FCSTD DOCUMENT  (FreeCAD 0.21R33771 (Git))
Label: drift2
License: All rights reserved
LicenseURL: https://en.wikipedia.org/wiki/All_rights_reserved
objects: Sketcher::SketchObject×5, Part::Loft×1
note: 6 computed .brp shape members not serialized (recipe doc carries the construction recipe); baked Part::Feature solids carry a one-line shape summary decoded from their .brp

FEATURE [Sketcher::SketchObject] Sketch  label="Sketch_s20_50x50"
  FullyConstrained = true
  sketch-geometry (5):
    g0: LineSegment StartX=-25 StartY=25 StartZ=0 EndX=-25 EndY=-25 EndZ=0
    g1: LineSegment StartX=-25 StartY=-25 StartZ=0 EndX=25 EndY=-25 EndZ=0
    g2: LineSegment StartX=25 StartY=-25 StartZ=0 EndX=25 EndY=25 EndZ=0
    g3: LineSegment StartX=25 StartY=25 StartZ=0 EndX=-25 EndY=25 EndZ=0
    g4: GeomPoint X=1e-16 Y=0 Z=0
  constraints (12):
    c: Coincident(g0,g1)
    c: Coincident(g1,g2)
    c: Coincident(g2,g3)
    c: Coincident(g3,g0)
    c: Horizontal(g1)
    c: Horizontal(g3)
    c: Vertical(g0)
    c: Vertical(g2)
    c: Symmetric(g1,g0,g4)
    c: Coincident(g4,g-1)
    c: Distance(g2) = 50
    c: Distance(g3) = 50
FEATURE [Sketcher::SketchObject] Sketch001  label="Sketch_s25_40x40"
  FullyConstrained = true
  Placement = pos=(0,0,5000) rot=(0,0,1;0rad)
  sketch-geometry (5):
    g0: LineSegment StartX=-20 StartY=20 StartZ=0 EndX=-20 EndY=-20 EndZ=0
    g1: LineSegment StartX=-20 StartY=-20 StartZ=0 EndX=20 EndY=-20 EndZ=0
    g2: LineSegment StartX=20 StartY=-20 StartZ=0 EndX=20 EndY=20 EndZ=0
    g3: LineSegment StartX=20 StartY=20 StartZ=0 EndX=-20 EndY=20 EndZ=0
    g4: GeomPoint X=1e-16 Y=1e-16 Z=0
  constraints (12):
    c: Coincident(g0,g1)
    c: Coincident(g1,g2)
    c: Coincident(g2,g3)
    c: Coincident(g3,g0)
    c: Horizontal(g1)
    c: Horizontal(g3)
    c: Vertical(g0)
    c: Vertical(g2)
    c: Symmetric(g1,g0,g4)
    c: Coincident(g4,g-1)
    c: Distance(g2) = 40
    c: Distance(g3) = 40
FEATURE [Sketcher::SketchObject] Sketch002  label="Sketch_s30_40x40"
  FullyConstrained = true
  Placement = pos=(0,0,10000) rot=(0,0,1;0rad)
  sketch-geometry (5):
    g0: LineSegment StartX=-20 StartY=20 StartZ=0 EndX=-20 EndY=-20 EndZ=0
    g1: LineSegment StartX=-20 StartY=-20 StartZ=0 EndX=20 EndY=-20 EndZ=0
    g2: LineSegment StartX=20 StartY=-20 StartZ=0 EndX=20 EndY=20 EndZ=0
    g3: LineSegment StartX=20 StartY=20 StartZ=0 EndX=-20 EndY=20 EndZ=0
    g4: GeomPoint X=-1e-16 Y=0 Z=0
  constraints (12):
    c: Coincident(g0,g1)
    c: Coincident(g1,g2)
    c: Coincident(g2,g3)
    c: Coincident(g3,g0)
    c: Horizontal(g1)
    c: Horizontal(g3)
    c: Vertical(g0)
    c: Vertical(g2)
    c: Symmetric(g1,g0,g4)
    c: Coincident(g4,g-1)
    c: Distance(g2) = 40
    c: Distance(g3) = 40
FEATURE [Sketcher::SketchObject] Sketch003  label="Sketch_s35_20x20"
  FullyConstrained = true
  Placement = pos=(0,0,15000) rot=(0,0,1;0rad)
  sketch-geometry (5):
    g0: LineSegment StartX=-10 StartY=10 StartZ=0 EndX=-10 EndY=-10 EndZ=0
    g1: LineSegment StartX=-10 StartY=-10 StartZ=0 EndX=10 EndY=-10 EndZ=0
    g2: LineSegment StartX=10 StartY=-10 StartZ=0 EndX=10 EndY=10 EndZ=0
    g3: LineSegment StartX=10 StartY=10 StartZ=0 EndX=-10 EndY=10 EndZ=0
    g4: GeomPoint X=0 Y=0 Z=0
  constraints (12):
    c: Coincident(g0,g1)
    c: Coincident(g1,g2)
    c: Coincident(g2,g3)
    c: Coincident(g3,g0)
    c: Horizontal(g1)
    c: Horizontal(g3)
    c: Vertical(g0)
    c: Vertical(g2)
    c: Symmetric(g1,g0,g4)
    c: Coincident(g4,g-1)
    c: Distance(g2) = 20
    c: Distance(g3) = 20
FEATURE [Sketcher::SketchObject] Sketch004  label="Sketch_s50_20x20"
  FullyConstrained = true
  Placement = pos=(0,0,30000) rot=(0,0,1;0rad)
  sketch-geometry (5):
    g0: LineSegment StartX=-10 StartY=10 StartZ=0 EndX=-10 EndY=-10 EndZ=0
    g1: LineSegment StartX=-10 StartY=-10 StartZ=0 EndX=10 EndY=-10 EndZ=0
    g2: LineSegment StartX=10 StartY=-10 StartZ=0 EndX=10 EndY=10 EndZ=0
    g3: LineSegment StartX=10 StartY=10 StartZ=0 EndX=-10 EndY=10 EndZ=0
    g4: GeomPoint X=0 Y=0 Z=0
  constraints (12):
    c: Coincident(g0,g1)
    c: Coincident(g1,g2)
    c: Coincident(g2,g3)
    c: Coincident(g3,g0)
    c: Horizontal(g1)
    c: Horizontal(g3)
    c: Vertical(g0)
    c: Vertical(g2)
    c: Symmetric(g1,g0,g4)
    c: Coincident(g4,g-1)
    c: Distance(g2) = 20
    c: Distance(g3) = 20
FEATURE [Part::Loft] Loft
  Closed = false
  MaxDegree = 5
  Ruled = true
  Sections = -> [Sketch,Sketch001,Sketch002,Sketch003,Sketch004]
  Solid = true
